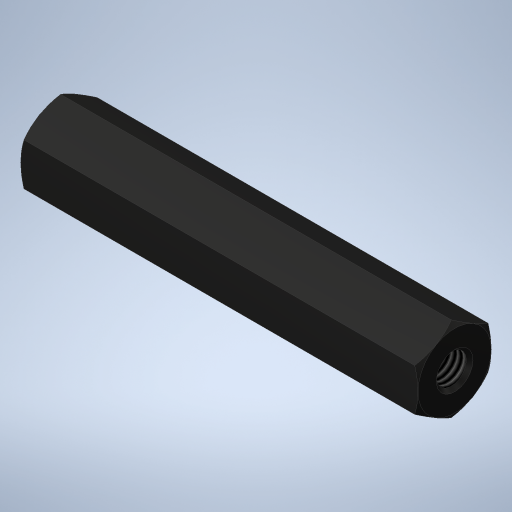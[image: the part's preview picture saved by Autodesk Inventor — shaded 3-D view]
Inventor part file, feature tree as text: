
AUTODESK INVENTOR PART (.ipt)
format: ipt  version: 2024.2 (Build 282272000, 272)  size: 285,184 bytes
history: native  units: mm
features: other x7, sketch x4, hole x2, revolve x1, extrude x1
ambient origin geometry x8: Origin, YZ Plane, XZ Plane, XY Plane, X Axis, Y Axis, Z Axis, Center Point
bodies: Solid1 (feature_tree)
feature tree (15):
  revolve  "Revolution1"  [1 undecoded]
  extrude  "Extrusion1"  TaperAngle=0.0deg  [1 undecoded]
  hole  "Hole1"  [1 undecoded]
  hole  "Hole2"  [1 undecoded]
  other  "C3_XY"
  other  "C3_YZ"
  other  "C3_ZX"
  other  "C3_X"
  other  "C3_Y"
  other  "C3_Z"
  other  "C3_Center"
  sketch  "Sketch_1"  dims[d0=360.0deg d1=32.5mm d2=0.0mm]
  sketch  "Sketch_2"  dims[d3=2.459mm d4=6.0mm d5=3.0mm d6=2.0mm d7=90.0deg d8=8.290148mm d9=120.0deg]
  sketch  "Sketch3"  dims[d10=2.459mm d11=6.0mm d12=3.0mm d13=2.0mm d14=90.0deg d15=8.290148mm d16=120.0deg d17=0.0mm]
  sketch  "Sketch4"
note: 4 required parameter values undecoded (feature->parameter linkage not recoverable at this tier; creation-order binding heuristic only, values carry confidence <= 0.55)